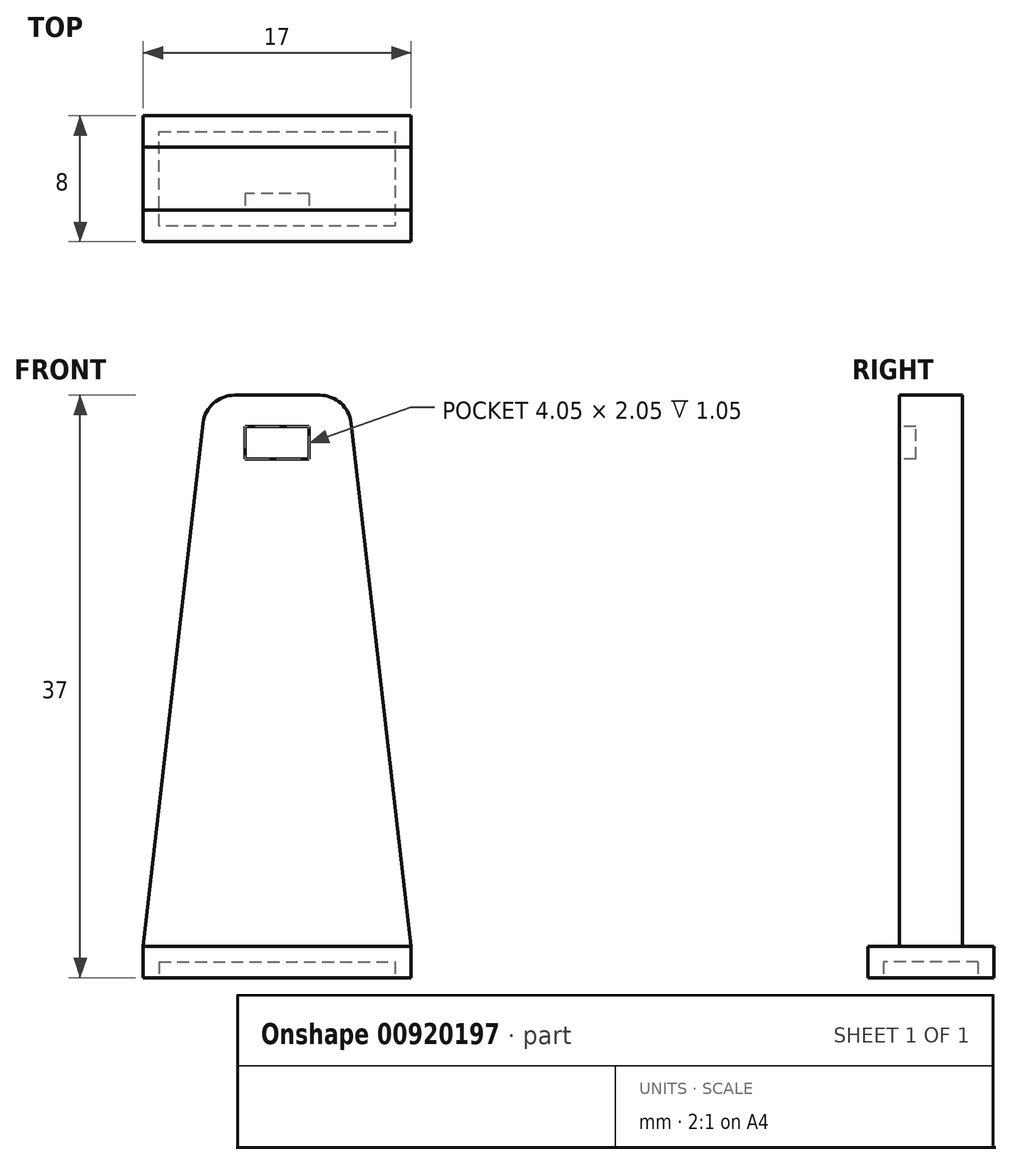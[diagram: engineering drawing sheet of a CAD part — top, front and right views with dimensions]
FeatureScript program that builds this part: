
annotation { "Feature Type Name" : "Feature", "Feature Type Description" : "" }
export const myFeature = defineFeature(function(context is Context, id is Id, definition is map)
    precondition{}
    {
        {
            var Q0;
            Q0=qCreatedBy(makeId("Top.planeOp"),FACE);
            var sketch = newSketch(context, id + "F0", { "sketchPlane" : qUnion([Q0])});
            skLineSegment(sketch, "E0.bottom", {"start": v(-4.5, 2) * mm, "end": v(4.5, 2) * mm});
            skLineSegment(sketch, "E0.top", {"start": v(-4.5, -2) * mm, "end": v(4.5, -2) * mm});
            skLineSegment(sketch, "E0.left", {"start": v(-4.5, 2) * mm, "end": v(-4.5, -2) * mm});
            skLineSegment(sketch, "E0.right", {"start": v(4.5, 2) * mm, "end": v(4.5, -2) * mm});
            skSolve(sketch);
        }
        {
            var Q0;
            Q0=qCreatedBy(makeId("Top.planeOp"),FACE);
            cPlane(context, id + "F1", {"entities" : qUnion([Q0]), "cplaneType" : CPlaneType.OFFSET, "offset" : 35 * mm, "oppositeDirection" : true, "width" : 150 * mm, "height" : 150 * mm});
        }
        {
            var Q0;
            Q0=qCreatedBy(id+"F1.planeOp",FACE);
            var sketch = newSketch(context, id + "F2", { "sketchPlane" : qUnion([Q0])});
            skLineSegment(sketch, "E1.bottom", {"start": v(8.5, -2) * mm, "end": v(-8.5, -2) * mm});
            skLineSegment(sketch, "E1.top", {"start": v(8.5, 2) * mm, "end": v(-8.5, 2) * mm});
            skLineSegment(sketch, "E1.left", {"start": v(8.5, -2) * mm, "end": v(8.5, 2) * mm});
            skLineSegment(sketch, "E1.right", {"start": v(-8.5, -2) * mm, "end": v(-8.5, 2) * mm});
            skPoint(sketch, "E1.middle", {"position": v(0, 0) * mm});
            skSolve(sketch);
        }
        {
            var Q0;
            Q0=makeQuery(id+"F0.imprint","IMPRINT",FACE,{"disambiguationData":[TD([[makeQuery(id+"F0.imprint","IMPRINT",EDGE,{"derivedFrom":sQuery(id+"F0.wireOp",EDGE,"E0.bottom")}),-1.0]])]});
            var Q1;
            Q1=makeQuery(id+"F2.imprint","IMPRINT",FACE,{"disambiguationData":[TD([[makeQuery(id+"F2.imprint","IMPRINT",EDGE,{"derivedFrom":sQuery(id+"F2.wireOp",EDGE,"E1.bottom")}),-1.0]])]});
            loft(context, id + "F3", {"sheetProfilesArray" : [{ "sheetProfileEntities" : qUnion([Q0]) }, { "sheetProfileEntities" : qUnion([Q1]) }]});
        }
        {
            var Q0;
            Q0=makeQuery(id+"F3.opLoft","CAP_FACE",FACE,{"disambiguationData":[OSD([makeQuery(id+"F2.imprint","IMPRINT",FACE,{"disambiguationData":[TD([[makeQuery(id+"F2.imprint","IMPRINT",EDGE,{"derivedFrom":sQuery(id+"F2.wireOp",EDGE,"E1.bottom")}),-1.0]])]})])],"isStart":true});
            extrude(context, id + "F4", {"entities" : qUnion([Q0]), "operationType" : NewBodyOperationType.ADD, "depth" : 2 * mm, "offsetDistance" : 25 * mm});
        }
        {
            var Q0;
            {var subQ0=sQuery(id+"F2.wireOp",EDGE,"E1.right");var subQ1=sQuery(id+"F2.wireOp",EDGE,"E1.left");var subQ2=sQuery(id+"F2.wireOp",EDGE,"E1.bottom");Q0=makeQuery(id+"F4.boolean.opBoolean","MERGE",FACE,{"derivedFrom":[makeQuery(id+"F3.opLoft","SWEPT_FACE",FACE,{"disambiguationData":[OSD([sQuery(id+"F0.wireOp",EDGE,"E0.top"),sQuery(id+"F0.wireOp",EDGE,"E0.left"),sQuery(id+"F0.wireOp",EDGE,"E0.right"),subQ2,subQ1,subQ0])]}),makeQuery(id+"F4.opExtrude","SWEPT_FACE",FACE,{"disambiguationData":[OSD([subQ2,subQ1,subQ0])]})]});}
            var sketch = newSketch(context, id + "F5", { "sketchPlane" : qUnion([Q0])});
            skLineSegment(sketch, "E2.bottom", {"start": v(-8.5, -37) * mm, "end": v(8.5, -37) * mm});
            skLineSegment(sketch, "E2.top", {"start": v(-8.5, -35) * mm, "end": v(8.5, -35) * mm});
            skLineSegment(sketch, "E2.left", {"start": v(-8.5, -37) * mm, "end": v(-8.5, -35) * mm});
            skLineSegment(sketch, "E2.right", {"start": v(8.5, -37) * mm, "end": v(8.5, -35) * mm});
            skSolve(sketch);
        }
        {
            var Q0;
            Q0=makeQuery(id+"F5.imprint","IMPRINT",FACE,{"disambiguationData":[TD([[makeQuery(id+"F5.imprint","IMPRINT",EDGE,{"derivedFrom":sQuery(id+"F5.wireOp",EDGE,"E2.bottom")}),-1.0]])]});
            extrude(context, id + "F6", {"entities" : qUnion([Q0]), "operationType" : NewBodyOperationType.ADD, "depth" : 2 * mm, "offsetDistance" : 25 * mm, "hasSecondDirection" : true, "secondDirectionOppositeDirection" : true, "secondDirectionDepth" : 6 * mm});
        }
        {
            var Q0;
            {var subQ0=sQuery(id+"F2.wireOp",EDGE,"E1.right");var subQ1=sQuery(id+"F2.wireOp",EDGE,"E1.left");var subQ2=sQuery(id+"F2.wireOp",EDGE,"E1.bottom");Q0=makeQuery(id+"F4.boolean.opBoolean","MERGE",FACE,{"derivedFrom":[makeQuery(id+"F3.opLoft","SWEPT_FACE",FACE,{"disambiguationData":[OSD([sQuery(id+"F0.wireOp",EDGE,"E0.top"),sQuery(id+"F0.wireOp",EDGE,"E0.left"),sQuery(id+"F0.wireOp",EDGE,"E0.right"),subQ2,subQ1,subQ0])]}),makeQuery(id+"F4.opExtrude","SWEPT_FACE",FACE,{"disambiguationData":[OSD([subQ2,subQ1,subQ0])]})]});}
            var sketch = newSketch(context, id + "F7", { "sketchPlane" : qUnion([Q0])});
            skLineSegment(sketch, "E3.bottom", {"start": v(2.03, -4.05) * mm, "end": v(-2.02, -4.05) * mm});
            skLineSegment(sketch, "E3.top", {"start": v(2.03, -2) * mm, "end": v(-2.02, -2) * mm});
            skLineSegment(sketch, "E3.left", {"start": v(2.03, -4.05) * mm, "end": v(2.03, -2) * mm});
            skLineSegment(sketch, "E3.right", {"start": v(-2.02, -4.05) * mm, "end": v(-2.02, -2) * mm});
            skPoint(sketch, "E3.middle", {"position": v(0, -3.02) * mm});
            skSolve(sketch);
        }
        {
            var Q0;
            Q0 = qSketchRegion(id + "F7", true);
            extrude(context, id + "F8", {"entities" : qUnion([Q0]), "operationType" : NewBodyOperationType.REMOVE, "oppositeDirection" : true, "depth" : 1.05 * mm, "offsetDistance" : 25 * mm});
        }
        {
            var Q0;
            Q0=makeQuery(id+"F6.boolean.opBoolean","MERGE",FACE,{"derivedFrom":[makeQuery(id+"F4.opExtrude","CAP_FACE",FACE,{"disambiguationData":[OSD([makeQuery(id+"F2.imprint","IMPRINT",FACE,{"disambiguationData":[TD([[makeQuery(id+"F2.imprint","IMPRINT",EDGE,{"derivedFrom":sQuery(id+"F2.wireOp",EDGE,"E1.bottom")}),-1.0]])]})])],"isStart":false}),makeQuery(id+"F6.opExtrude","SWEPT_FACE",FACE,{"disambiguationData":[OSD([sQuery(id+"F5.wireOp",EDGE,"E2.bottom")])]})]});
            var sketch = newSketch(context, id + "F9", { "sketchPlane" : qUnion([Q0])});
            skLineSegment(sketch, "E4.0", {"start": v(7.5, -3) * mm, "end": v(7.5, 3) * mm});
            skLineSegment(sketch, "E4.1", {"start": v(-7.5, -3) * mm, "end": v(7.5, -3) * mm});
            skLineSegment(sketch, "E4.2", {"start": v(-7.5, 3) * mm, "end": v(-7.5, -3) * mm});
            skLineSegment(sketch, "E4.3", {"start": v(7.5, 3) * mm, "end": v(-7.5, 3) * mm});
            skSolve(sketch);
        }
        {
            var Q0;
            Q0 = qSketchRegion(id + "F9", true);
            extrude(context, id + "F10", {"entities" : qUnion([Q0]), "operationType" : NewBodyOperationType.REMOVE, "oppositeDirection" : true, "depth" : 1 * mm, "offsetDistance" : 25 * mm});
        }
        {
            var Q0;
            Q0=makeQuery(id+"F3.opLoft","MID_CAP_EDGE",EDGE,{"disambiguationData":[OSD([sQuery(id+"F0.wireOp",EDGE,"E0.bottom"),sQuery(id+"F0.wireOp",EDGE,"E0.top"),sQuery(id+"F0.wireOp",EDGE,"E0.left")])],"capPos":0.0});
            var Q1;
            Q1=makeQuery(id+"F3.opLoft","MID_CAP_EDGE",EDGE,{"disambiguationData":[OSD([sQuery(id+"F0.wireOp",EDGE,"E0.bottom"),sQuery(id+"F0.wireOp",EDGE,"E0.top"),sQuery(id+"F0.wireOp",EDGE,"E0.right")])],"capPos":0.0});
            fillet(context, id + "F11", {"entities" : qUnion([Q0, Q1]), "radius" : 2 * mm, "tangentPropagation" : true, "allowEdgeOverflow" : false});
        }
    });
